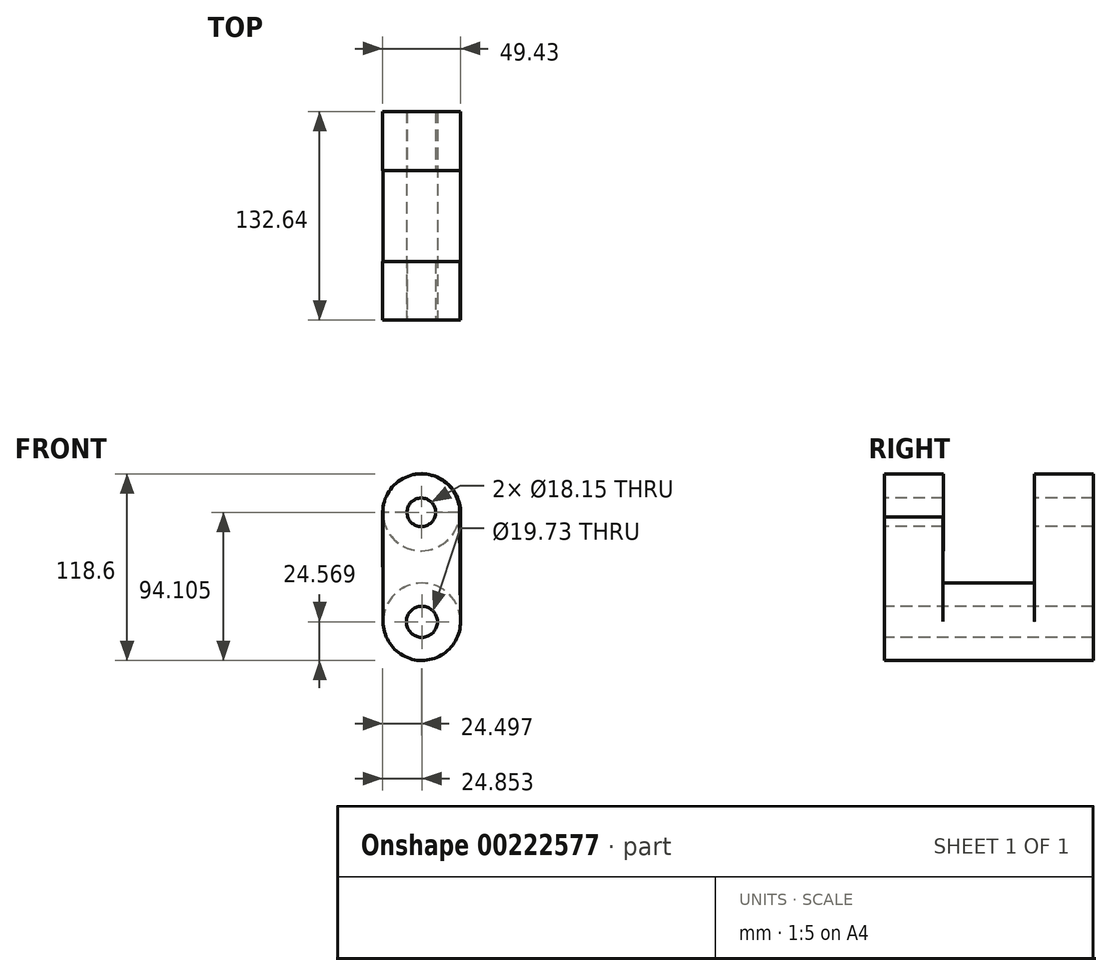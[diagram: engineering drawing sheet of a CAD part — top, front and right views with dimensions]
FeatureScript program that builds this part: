
annotation { "Feature Type Name" : "Feature", "Feature Type Description" : "" }
export const myFeature = defineFeature(function(context is Context, id is Id, definition is map)
    precondition{}
    {
        {
            var Q0;
            Q0=qCreatedBy(makeId("Front.planeOp"),FACE);
            var sketch = newSketch(context, id + "F0", { "sketchPlane" : qUnion([Q0])});
            skCircle(sketch, "E0", {"center": v(-8.2, -21.13) * mm, "radius": 24.57 * mm});
            skSolve(sketch);
        }
        {
            var Q0;
            Q0 = qSketchRegion(id + "F0", true);
            extrude(context, id + "F1", {"entities" : qUnion([Q0]), "oppositeDirection" : true, "depth" : 132.64 * mm});
        }
        {
            var Q0;
            Q0=makeQuery(id+"F1.opExtrude","CAP_FACE",FACE,{"disambiguationData":[OSD([sQuery(id+"F0.wireOp",EDGE,"E0")])],"isStart":true});
            var sketch = newSketch(context, id + "F2", { "sketchPlane" : qUnion([Q0])});
            skLineSegment(sketch, "E1", {"start": v(-32.78, -21.32) * mm, "end": v(-32.78, 48.4) * mm});
            skLineSegment(sketch, "E2", {"start": v(-32.78, 48.4) * mm, "end": v(15.65, 48.4) * mm});
            skLineSegment(sketch, "E3", {"start": v(15.65, 48.4) * mm, "end": v(16.37, -20.88) * mm});
            skArc(sketch, "E4", {"start": v(16.37, -20.88) * mm, "mid": v(-8.43, 3.44) * mm, "end": v(-32.78, -21.32) * mm});
            skSolve(sketch);
        }
        {
            var Q0;
            Q0 = qSketchRegion(id + "F2", true);
            extrude(context, id + "F3", {"entities" : qUnion([Q0]), "operationType" : NewBodyOperationType.ADD, "oppositeDirection" : true, "depth" : 37.13 * mm});
        }
        {
            var Q0;
            Q0=makeQuery(id+"F1.opExtrude","CAP_FACE",FACE,{"disambiguationData":[OSD([sQuery(id+"F0.wireOp",EDGE,"E0")])],"isStart":false});
            var sketch = newSketch(context, id + "F4", { "sketchPlane" : qUnion([Q0])});
            skLineSegment(sketch, "E5", {"start": v(-16.37, -21.24) * mm, "end": v(-16.37, 48.19) * mm});
            skLineSegment(sketch, "E6", {"start": v(-16.37, 48.19) * mm, "end": v(33.06, 48.19) * mm});
            skLineSegment(sketch, "E7", {"start": v(33.06, 48.19) * mm, "end": v(32.78, -21.23) * mm});
            skArc(sketch, "E8", {"start": v(32.78, -21.23) * mm, "mid": v(8.2, 3.33) * mm, "end": v(-16.37, -21.24) * mm});
            skSolve(sketch);
        }
        {
            var Q0;
            Q0 = qSketchRegion(id + "F4", true);
            extrude(context, id + "F5", {"entities" : qUnion([Q0]), "operationType" : NewBodyOperationType.ADD, "oppositeDirection" : true, "depth" : 37.35 * mm});
        }
        {
            var Q0;
            Q0=makeQuery(id+"F3.boolean.opBoolean","MERGE",FACE,{"derivedFrom":[makeQuery(id+"F1.opExtrude","CAP_FACE",FACE,{"disambiguationData":[OSD([sQuery(id+"F0.wireOp",EDGE,"E0")])],"isStart":true}),makeQuery(id+"F3.opExtrude","CAP_FACE",FACE,{"disambiguationData":[OSD([sQuery(id+"F2.wireOp",EDGE,"E1"),sQuery(id+"F2.wireOp",EDGE,"E2"),sQuery(id+"F2.wireOp",EDGE,"E3"),sQuery(id+"F2.wireOp",EDGE,"E4")])],"isStart":true})]});
            var sketch = newSketch(context, id + "F6", { "sketchPlane" : qUnion([Q0])});
            skCircle(sketch, "E9", {"center": v(-8.56, 48.4) * mm, "radius": 24.45 * mm});
            skSolve(sketch);
        }
        {
            var Q0;
            Q0 = qSketchRegion(id + "F6", true);
            extrude(context, id + "F7", {"entities" : qUnion([Q0]), "operationType" : NewBodyOperationType.ADD, "oppositeDirection" : true, "depth" : 37.25 * mm});
        }
        {
            var Q0;
            Q0=makeQuery(id+"F5.boolean.opBoolean","MERGE",FACE,{"derivedFrom":[makeQuery(id+"F1.opExtrude","CAP_FACE",FACE,{"disambiguationData":[OSD([sQuery(id+"F0.wireOp",EDGE,"E0")])],"isStart":false}),makeQuery(id+"F5.opExtrude","CAP_FACE",FACE,{"disambiguationData":[OSD([sQuery(id+"F4.wireOp",EDGE,"E5"),sQuery(id+"F4.wireOp",EDGE,"E6"),sQuery(id+"F4.wireOp",EDGE,"E7"),sQuery(id+"F4.wireOp",EDGE,"E8")])],"isStart":true})]});
            var sketch = newSketch(context, id + "F8", { "sketchPlane" : qUnion([Q0])});
            skArc(sketch, "E10", {"start": v(33.06, 48.19) * mm, "mid": v(8.35, 72.9) * mm, "end": v(-16.37, 48.19) * mm});
            skSolve(sketch);
        }
        {
            var Q0;
            Q0=makeQuery(id+"F8.imprint","IMPRINT",FACE,{"disambiguationData":[TD([[makeQuery(id+"F8.imprint","IMPRINT",EDGE,{"derivedFrom":sQuery(id+"F8.wireOp",EDGE,"E10")}),1.0]])]});
            extrude(context, id + "F9", {"entities" : qUnion([Q0]), "operationType" : NewBodyOperationType.ADD, "oppositeDirection" : true, "depth" : 37.5 * mm});
        }
        {
            var Q0;
            Q0=makeQuery(id+"F7.boolean.opBoolean","MERGE",FACE,{"derivedFrom":[makeQuery(id+"F3.boolean.opBoolean","MERGE",FACE,{"derivedFrom":[makeQuery(id+"F1.opExtrude","CAP_FACE",FACE,{"disambiguationData":[OSD([sQuery(id+"F0.wireOp",EDGE,"E0")])],"isStart":true}),makeQuery(id+"F3.opExtrude","CAP_FACE",FACE,{"disambiguationData":[OSD([sQuery(id+"F2.wireOp",EDGE,"E1"),sQuery(id+"F2.wireOp",EDGE,"E2"),sQuery(id+"F2.wireOp",EDGE,"E3"),sQuery(id+"F2.wireOp",EDGE,"E4")])],"isStart":true})]}),makeQuery(id+"F7.opExtrude","CAP_FACE",FACE,{"disambiguationData":[OSD([sQuery(id+"F6.wireOp",EDGE,"E9")])],"isStart":true})]});
            var sketch = newSketch(context, id + "F10", { "sketchPlane" : qUnion([Q0])});
            skCircle(sketch, "E11", {"center": v(-8.56, 48.4) * mm, "radius": 9.08 * mm});
            skSolve(sketch);
        }
        {
            var Q0;
            Q0 = qSketchRegion(id + "F10", true);
            extrude(context, id + "F11", {"entities" : qUnion([Q0]), "operationType" : NewBodyOperationType.REMOVE, "endBound" : BoundingType.THROUGH_ALL, "oppositeDirection" : true, "depth" : 25.4 * mm});
        }
        {
            var Q0;
            Q0=makeQuery(id+"F7.boolean.opBoolean","MERGE",FACE,{"derivedFrom":[makeQuery(id+"F3.boolean.opBoolean","MERGE",FACE,{"derivedFrom":[makeQuery(id+"F1.opExtrude","CAP_FACE",FACE,{"disambiguationData":[OSD([sQuery(id+"F0.wireOp",EDGE,"E0")])],"isStart":true}),makeQuery(id+"F3.opExtrude","CAP_FACE",FACE,{"disambiguationData":[OSD([sQuery(id+"F2.wireOp",EDGE,"E1"),sQuery(id+"F2.wireOp",EDGE,"E2"),sQuery(id+"F2.wireOp",EDGE,"E3"),sQuery(id+"F2.wireOp",EDGE,"E4")])],"isStart":true})]}),makeQuery(id+"F7.opExtrude","CAP_FACE",FACE,{"disambiguationData":[OSD([sQuery(id+"F6.wireOp",EDGE,"E9")])],"isStart":true})]});
            var sketch = newSketch(context, id + "F12", { "sketchPlane" : qUnion([Q0])});
            skCircle(sketch, "E12", {"center": v(-8.2, -21.13) * mm, "radius": 9.87 * mm});
            skSolve(sketch);
        }
        {
            var Q0;
            Q0 = qSketchRegion(id + "F12", true);
            extrude(context, id + "F13", {"entities" : qUnion([Q0]), "operationType" : NewBodyOperationType.REMOVE, "endBound" : BoundingType.THROUGH_ALL, "oppositeDirection" : true, "depth" : 25.4 * mm});
        }
    });
